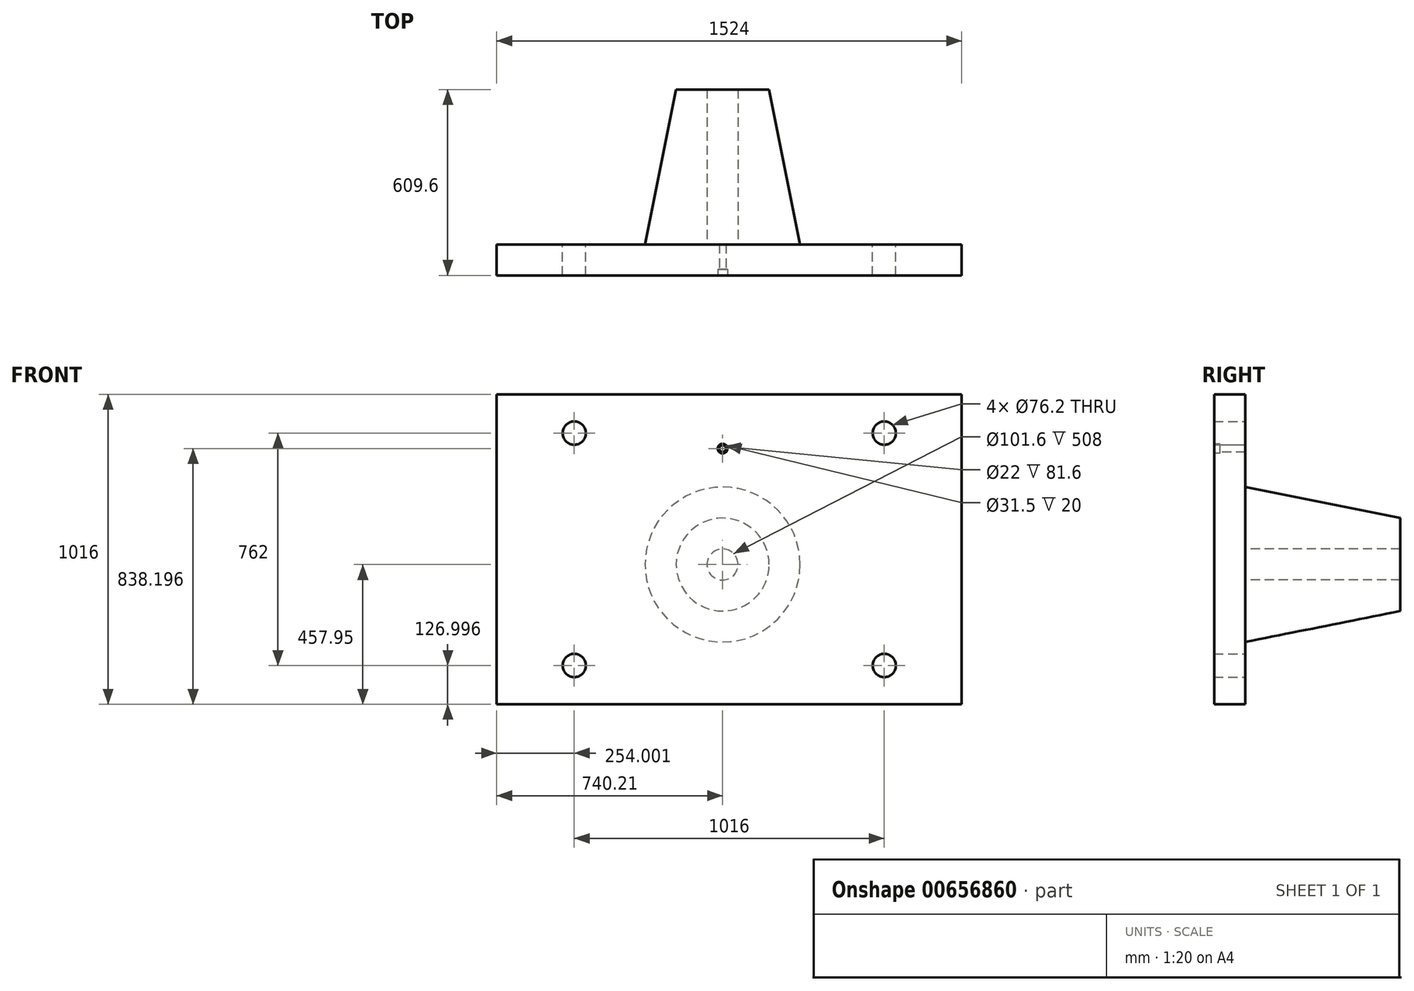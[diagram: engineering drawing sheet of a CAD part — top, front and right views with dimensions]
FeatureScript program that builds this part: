
annotation { "Feature Type Name" : "Feature", "Feature Type Description" : "" }
export const myFeature = defineFeature(function(context is Context, id is Id, definition is map)
    precondition{}
    {
        {
            var Q0;
            Q0=qCreatedBy(makeId("Front.planeOp"),FACE);
            var sketch = newSketch(context, id + "F0", { "sketchPlane" : qUnion([Q0])});
            skLineSegment(sketch, "E0.bottom", {"start": v(-740.2, 558.05) * mm, "end": v(783.8, 558.05) * mm});
            skLineSegment(sketch, "E0.top", {"start": v(-740.2, -457.95) * mm, "end": v(783.8, -457.95) * mm});
            skLineSegment(sketch, "E0.left", {"start": v(-740.2, 558.05) * mm, "end": v(-740.2, -457.95) * mm});
            skLineSegment(sketch, "E0.right", {"start": v(783.8, 558.05) * mm, "end": v(783.8, -457.95) * mm});
            skCircle(sketch, "E1", {"center": v(529.8, 431.05) * mm, "radius": 38.1 * mm});
            skCircle(sketch, "E2", {"center": v(-486.2, 431.05) * mm, "radius": 38.1 * mm});
            skCircle(sketch, "E3", {"center": v(529.8, -330.95) * mm, "radius": 38.1 * mm});
            skCircle(sketch, "E4", {"center": v(-486.2, -330.95) * mm, "radius": 38.1 * mm});
            skSolve(sketch);
        }
        {
            var Q0;
            Q0 = qSketchRegion(id + "F0", true);
            extrude(context, id + "F1", {"entities" : qUnion([Q0]), "depth" : 101.6 * mm, "offsetDistance" : 25.4 * mm});
        }
        {
            var Q0;
            Q0=qCreatedBy(makeId("Top.planeOp"),FACE);
            var sketch = newSketch(context, id + "F2", { "sketchPlane" : qUnion([Q0])});
            skLineSegment(sketch, "E5", {"start": v(50.8, 0) * mm, "end": v(254, 0) * mm});
            skLineSegment(sketch, "E6", {"start": v(50.8, 0) * mm, "end": v(50.8, 508) * mm});
            skLineSegment(sketch, "E7", {"start": v(50.8, 508) * mm, "end": v(152.4, 508) * mm});
            skLineSegment(sketch, "E8", {"start": v(152.4, 508) * mm, "end": v(254, 0) * mm});
            skLineSegment(sketch, "E9", {"start": v(0, 0) * mm, "end": v(0, 280.52) * mm});
            skSolve(sketch);
        }
        {
            var Q0;
            Q0=makeQuery(id+"F2.imprint","IMPRINT",FACE,{"disambiguationData":[TD([[makeQuery(id+"F2.imprint","IMPRINT",EDGE,{"derivedFrom":sQuery(id+"F2.wireOp",EDGE,"E5")}),1.0]])]});
            var Q1;
            Q1=sQuery(id+"F2.wireOp",EDGE,"E9");
            revolve(context, id + "F3", {"operationType" : NewBodyOperationType.ADD, "entities" : qUnion([Q0]), "axis" : qUnion([Q1]), "revolveType" : RevolveType.FULL});
        }
        {
            var Q0;
            Q0=makeQuery(id+"F1.opExtrude","CAP_FACE",FACE,{"disambiguationData":[OSD([sQuery(id+"F0.wireOp",EDGE,"E0.bottom"),sQuery(id+"F0.wireOp",EDGE,"E0.top"),sQuery(id+"F0.wireOp",EDGE,"E0.left"),sQuery(id+"F0.wireOp",EDGE,"E0.right"),sQuery(id+"F0.wireOp",EDGE,"E1"),sQuery(id+"F0.wireOp",EDGE,"E2"),sQuery(id+"F0.wireOp",EDGE,"E3"),sQuery(id+"F0.wireOp",EDGE,"E4")])],"isStart":false});
            var sketch = newSketch(context, id + "F4", { "sketchPlane" : qUnion([Q0])});
            skPoint(sketch, "E10", {"position": v(0, 380.25) * mm});
            skSolve(sketch);
        }
        {
            var Q0;
            Q0=sQuery(id+"F4.wireOp",VERTEX,"E10");
            var Q1;
            Q1=makeQuery(id+"F1.opExtrude","SWEPT_BODY",BODY,{"disambiguationData":[OSD([sQuery(id+"F0.wireOp",EDGE,"E0.bottom"),sQuery(id+"F0.wireOp",EDGE,"E0.top"),sQuery(id+"F0.wireOp",EDGE,"E0.left"),sQuery(id+"F0.wireOp",EDGE,"E0.right"),sQuery(id+"F0.wireOp",EDGE,"E1"),sQuery(id+"F0.wireOp",EDGE,"E2"),sQuery(id+"F0.wireOp",EDGE,"E3"),sQuery(id+"F0.wireOp",EDGE,"E4")])]});
            hole(context, id + "F5", {"style" : HoleStyle.C_BORE, "endStyle" : HoleEndStyle.THROUGH, "standardTappedOrClearance" : lookupTablePath({ "standard" : "ISO", "fit" : "Normal", "size" : "M20", "type" : "Clearance" }), "standardBlindInLast" : lookupTablePath({ "fit" : "Standard", "standard" : "ISO", "size" : "M20", "type" : "Clearance" }), "holeDiameter" : 22 * mm, "cBoreDiameter" : 31.5 * mm, "cBoreDepth" : 20 * mm, "majorDiameter" : 6.35 * mm, "isTappedThrough" : true, "tappedDepth" : 12.7 * mm, "tapClearance" : 3, "locations" : qUnion([Q0]), "scope" : qUnion([Q1])});
        }
    });
